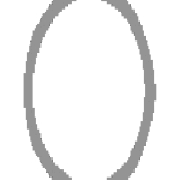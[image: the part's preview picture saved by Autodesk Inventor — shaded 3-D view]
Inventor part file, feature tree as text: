
AUTODESK INVENTOR PART (.ipt)
format: ipt  version: 2021 (Build 250183000, 183)  size: 109,568 bytes
history: native  units: in
note: dims shown in document units (in); Inventor stores cm internally (conversion verified against a paired STEP export)
features: other x4, sketch x3, plane x1
ambient origin geometry x8: Origin, YZ Plane, XZ Plane, XY Plane, X Axis, Y Axis, Z Axis, Center Point
bodies: Solid1 (feature_tree), Body (feature_tree)
feature tree (8):
  other  "Driven Length"
  other  "Frame Generator"
  other  "Start Plane"
  other  "End Plane"
  sketch  "Sketch"  dims[d2=20.0in d4=-0.0in d5=20.0in d6=0.12in d7=0.0in d8=90.0deg d9=20.0in]
  sketch  "Sketch2"  dims[d0=1.0in]
  plane  "Work Plane3"
  sketch  "Sketch3"  dims[d1=0.065in]
